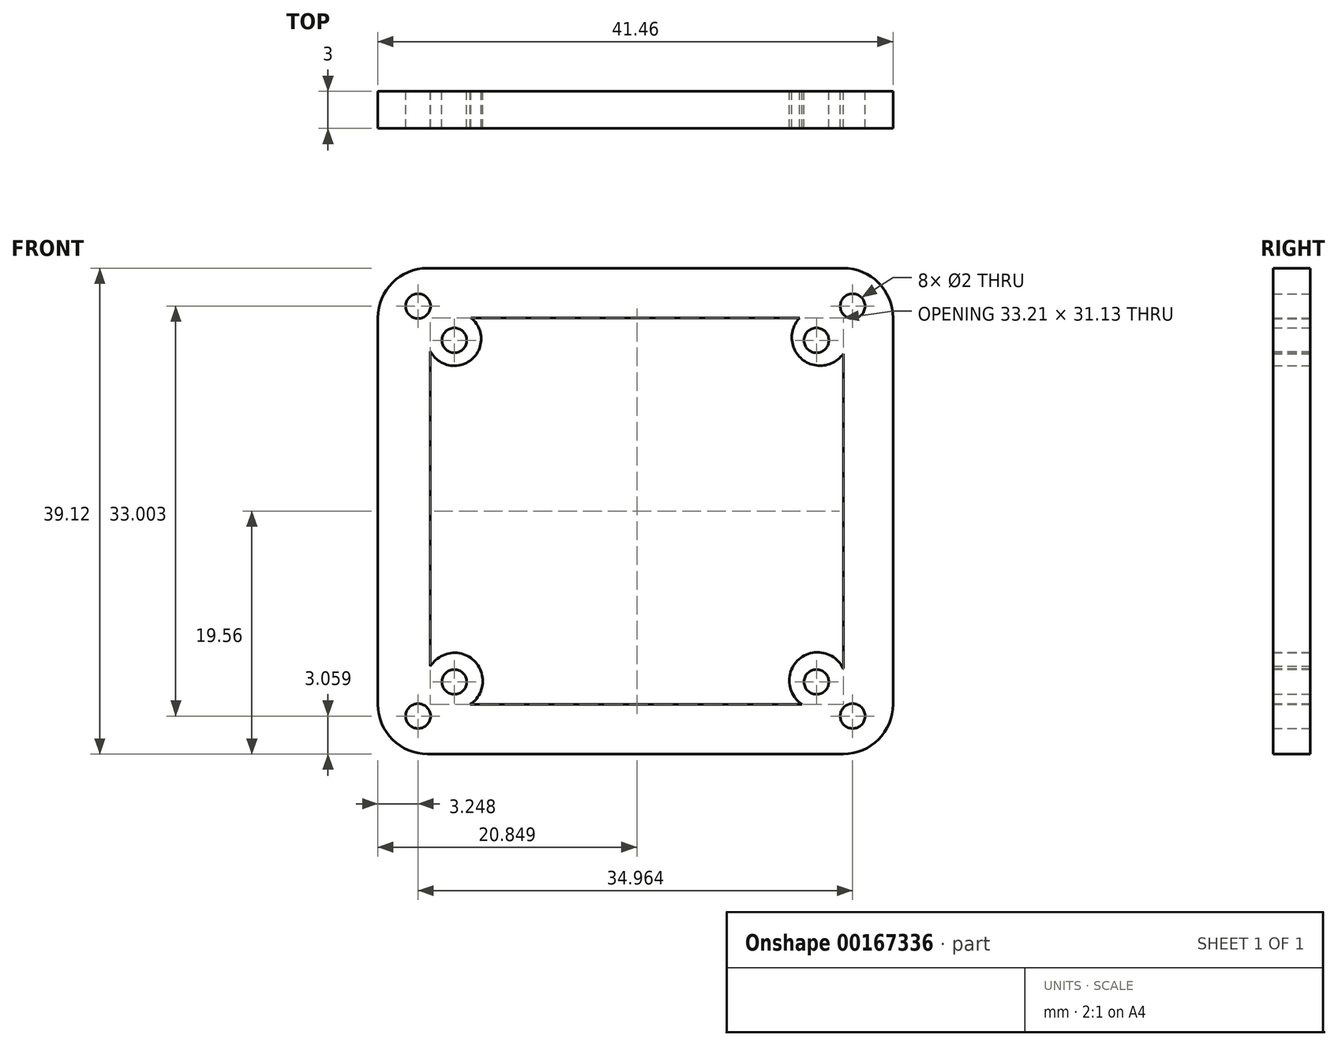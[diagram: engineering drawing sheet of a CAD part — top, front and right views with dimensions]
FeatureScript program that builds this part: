
annotation { "Feature Type Name" : "Feature", "Feature Type Description" : "" }
export const myFeature = defineFeature(function(context is Context, id is Id, definition is map)
    precondition{}
    {
        {
            var Q0;
            Q0=qCreatedBy(makeId("Front.planeOp"),FACE);
            var sketch = newSketch(context, id + "F0", { "sketchPlane" : qUnion([Q0])});
            skLineSegment(sketch, "E0.bottom", {"start": v(-16.73, 19.56) * mm, "end": v(16.73, 19.56) * mm});
            skLineSegment(sketch, "E0.top", {"start": v(-16.73, -19.56) * mm, "end": v(16.73, -19.56) * mm});
            skLineSegment(sketch, "E0.left", {"start": v(-20.73, 15.56) * mm, "end": v(-20.73, -15.56) * mm});
            skLineSegment(sketch, "E0.right", {"start": v(20.73, 15.56) * mm, "end": v(20.73, -15.56) * mm});
            skLineSegment(sketch, "E1", {"start": v(-20.73, 19.56) * mm, "end": v(20.73, -19.56) * mm, "construction": true});
            skLineSegment(sketch, "E2", {"start": v(20.73, 19.56) * mm, "end": v(-20.73, -19.56) * mm, "construction": true});
            skCircle(sketch, "E3", {"center": v(-17.48, -16.5) * mm, "radius": 1 * mm});
            skCircle(sketch, "E4", {"center": v(-17.48, 16.5) * mm, "radius": 1 * mm});
            skCircle(sketch, "E5", {"center": v(17.48, 16.5) * mm, "radius": 1 * mm});
            skCircle(sketch, "E6", {"center": v(17.48, -16.5) * mm, "radius": 1 * mm});
            skPoint(sketch, "E7.visualSharp", {"position": v(-20.73, 19.56) * mm});
            skArc(sketch, "E7.filletArc", {"start": v(-16.73, 19.56) * mm, "mid": v(-19.55, 18.4) * mm, "end": v(-20.73, 15.56) * mm});
            skPoint(sketch, "E8.visualSharp", {"position": v(20.73, 19.56) * mm});
            skArc(sketch, "E8.filletArc", {"start": v(20.73, 15.56) * mm, "mid": v(19.55, 18.4) * mm, "end": v(16.73, 19.56) * mm});
            skPoint(sketch, "E9.visualSharp", {"position": v(20.73, -19.56) * mm});
            skArc(sketch, "E9.filletArc", {"start": v(16.73, -19.56) * mm, "mid": v(19.55, -18.4) * mm, "end": v(20.73, -15.56) * mm});
            skPoint(sketch, "E10.visualSharp", {"position": v(-20.73, -19.56) * mm});
            skArc(sketch, "E10.filletArc", {"start": v(-20.73, -15.56) * mm, "mid": v(-19.55, -18.4) * mm, "end": v(-16.73, -19.56) * mm});
            skLineSegment(sketch, "E11.bottom", {"start": v(-13.23, 15.56) * mm, "end": v(13.22, 15.56) * mm});
            skLineSegment(sketch, "E11.top", {"start": v(-13.3, -15.56) * mm, "end": v(13.42, -15.56) * mm});
            skLineSegment(sketch, "E11.left", {"start": v(-16.49, 12.87) * mm, "end": v(-16.49, -12.5) * mm});
            skLineSegment(sketch, "E11.right", {"start": v(16.73, 12.67) * mm, "end": v(16.73, -12.67) * mm});
            skCircle(sketch, "E12", {"center": v(-14.57, 13.75) * mm, "radius": 1 * mm});
            skCircle(sketch, "E13", {"center": v(14.57, 13.75) * mm, "radius": 1 * mm});
            skCircle(sketch, "E14", {"center": v(14.57, -13.75) * mm, "radius": 1 * mm});
            skCircle(sketch, "E15", {"center": v(-14.57, -13.75) * mm, "radius": 1 * mm});
            skArc(sketch, "E16", {"start": v(13.22, 15.56) * mm, "mid": v(13.42, 12.23) * mm, "end": v(16.73, 12.67) * mm});
            skArc(sketch, "E17", {"start": v(16.73, -12.67) * mm, "mid": v(13.16, -11.93) * mm, "end": v(13.42, -15.56) * mm});
            skPoint(sketch, "E17.endSnap0", {"position": v(13.42, 12.23) * mm});
            skArc(sketch, "E18", {"start": v(-13.3, -15.56) * mm, "mid": v(-13, -12.02) * mm, "end": v(-16.52, -12.54) * mm});
            skArc(sketch, "E19", {"start": v(-16.49, 12.87) * mm, "mid": v(-13.2, 12.2) * mm, "end": v(-13.23, 15.56) * mm});
            skPoint(sketch, "E20.orphan", {"position": v(-16.49, 15.56) * mm});
            skLineSegment(sketch, "E21.trimOffspring", {"start": v(16.49, -15.56) * mm, "end": v(16.73, -15.56) * mm});
            skLineSegment(sketch, "E22.trimOffspring", {"start": v(16.49, 15.56) * mm, "end": v(16.73, 15.56) * mm});
            skSolve(sketch);
        }
        {
            var Q0;
            Q0=makeQuery(id+"F0.imprint","IMPRINT",FACE,{"disambiguationData":[TD([[makeQuery(id+"F0.imprint","IMPRINT",EDGE,{"derivedFrom":sQuery(id+"F0.wireOp",EDGE,"E0.bottom")}),-1.0]])]});
            extrude(context, id + "F1", {"entities" : qUnion([Q0]), "depth" : 3 * mm});
        }
    });
